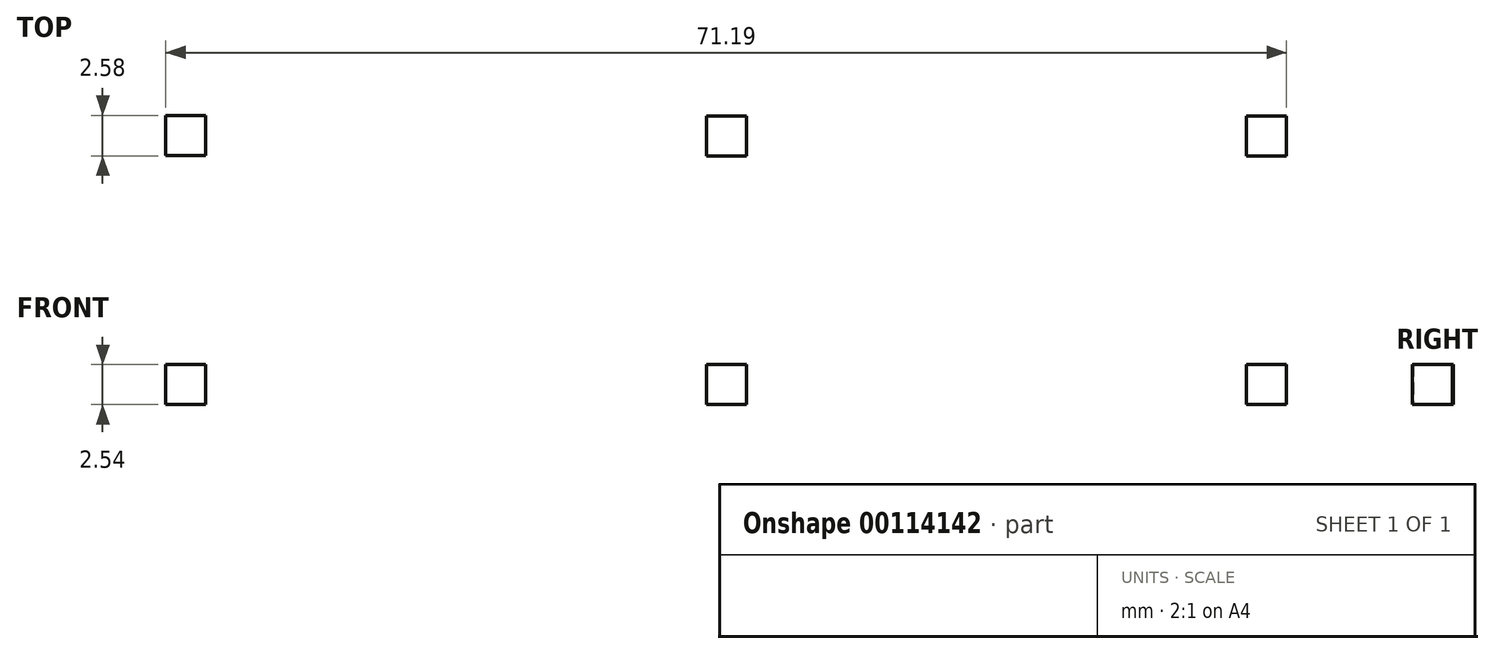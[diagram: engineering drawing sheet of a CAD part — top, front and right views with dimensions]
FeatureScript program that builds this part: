
annotation { "Feature Type Name" : "Feature", "Feature Type Description" : "" }
export const myFeature = defineFeature(function(context is Context, id is Id, definition is map)
    precondition{}
    {
        {
            var Q0;
            Q0=qCreatedBy(makeId("Top.planeOp"),FACE);
            var sketch = newSketch(context, id + "F0", { "sketchPlane" : qUnion([Q0])});
            skLineSegment(sketch, "E0.bottom", {"start": v(-0.93, 1.61) * mm, "end": v(1.6, 1.61) * mm});
            skLineSegment(sketch, "E0.top", {"start": v(-0.93, -0.93) * mm, "end": v(1.6, -0.93) * mm});
            skLineSegment(sketch, "E0.left", {"start": v(-0.93, 1.61) * mm, "end": v(-0.93, -0.93) * mm});
            skLineSegment(sketch, "E0.right", {"start": v(1.6, 1.61) * mm, "end": v(1.6, -0.93) * mm});
            skSolve(sketch);
        }
        {
            var Q0;
            Q0 = qSketchRegion(id + "F0", true);
            extrude(context, id + "F1", {"entities" : qUnion([Q0]), "depth" : 2.54 * mm});
        }
        {
            var Q0;
            Q0=qCreatedBy(makeId("Top.planeOp"),FACE);
            var sketch = newSketch(context, id + "F2", { "sketchPlane" : qUnion([Q0])});
            skLineSegment(sketch, "E1", {"start": v(1.68, -0.97) * mm, "end": v(33.43, -0.97) * mm});
            skLineSegment(sketch, "E2.bottom", {"start": v(33.43, -0.97) * mm, "end": v(35.97, -0.97) * mm});
            skLineSegment(sketch, "E2.top", {"start": v(33.43, 1.57) * mm, "end": v(35.97, 1.57) * mm});
            skLineSegment(sketch, "E2.left", {"start": v(33.43, -0.97) * mm, "end": v(33.43, 1.57) * mm});
            skLineSegment(sketch, "E2.right", {"start": v(35.97, -0.97) * mm, "end": v(35.97, 1.57) * mm});
            skSolve(sketch);
        }
        {
            var Q0;
            Q0=makeQuery(id+"F2.imprint","IMPRINT",FACE,{"disambiguationData":[TD([[makeQuery(id+"F2.imprint","IMPRINT",EDGE,{"derivedFrom":sQuery(id+"F2.wireOp",EDGE,"E2.bottom")}),1.0]])]});
            extrude(context, id + "F3", {"entities" : qUnion([Q0]), "depth" : 2.54 * mm});
        }
        {
            var Q0;
            Q0=qCreatedBy(makeId("Top.planeOp"),FACE);
            var sketch = newSketch(context, id + "F4", { "sketchPlane" : qUnion([Q0])});
            skLineSegment(sketch, "E3.bottom", {"start": v(67.72, -0.97) * mm, "end": v(70.26, -0.97) * mm});
            skLineSegment(sketch, "E3.top", {"start": v(67.72, 1.57) * mm, "end": v(70.26, 1.57) * mm});
            skLineSegment(sketch, "E3.left", {"start": v(67.72, -0.97) * mm, "end": v(67.72, 1.57) * mm});
            skLineSegment(sketch, "E3.right", {"start": v(70.26, -0.97) * mm, "end": v(70.26, 1.57) * mm});
            skSolve(sketch);
        }
        {
            var Q0;
            Q0=makeQuery(id+"F4.imprint","IMPRINT",FACE,{"disambiguationData":[TD([[makeQuery(id+"F4.imprint","IMPRINT",EDGE,{"derivedFrom":sQuery(id+"F4.wireOp",EDGE,"E3.bottom")}),1.0]])]});
            extrude(context, id + "F5", {"entities" : qUnion([Q0]), "depth" : 2.54 * mm});
        }
        {
            var Q0;
            Q0=qCreatedBy(makeId("Top.planeOp"),FACE);
            var sketch = newSketch(context, id + "F6", { "sketchPlane" : qUnion([Q0])});
            skText(sketch, "E4", { "text": "= Substrate              =  Spacer Layer        = Structural Layer", "fontName": "OpenSans-Bold.ttf"});
            const initialGuessF6  = {"E4": [0.00542, -0.0009, 1, 0, 0.00262]};
            skSetInitialGuess(sketch, initialGuessF6);
            skSolve(sketch);
        }
        {
            var Q0;
            Q0 = qSketchRegion(id + "F6", true);
            var Q1;
            Q1 = qConstructionFilter(qBodyType(qCreatedBy(id + "F6" ,EDGE), BodyType.WIRE), ConstructionObject.NO);
            extrude(context, id + "F7", {"entities" : qUnion([Q0]), "bodyType" : ToolBodyType.SURFACE, "operationType" : NewBodyOperationType.ADD, "surfaceEntities" : qUnion([Q1]), "depth" : 0.03 * mm});
        }
    });
